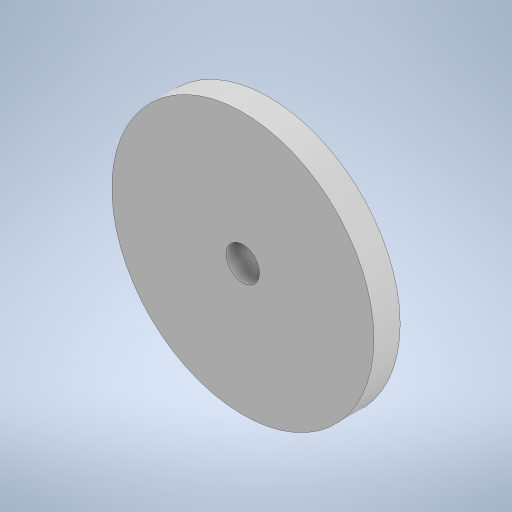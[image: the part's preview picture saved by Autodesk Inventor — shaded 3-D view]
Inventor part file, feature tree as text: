
AUTODESK INVENTOR PART (.ipt)
format: ipt  version: 2024 (Build 280153000, 153)  size: 210,944 bytes
history: native  units: mm
features: extrude x1, sketch x1
ambient origin geometry x8: Origin, YZ Plane, XZ Plane, XY Plane, X Axis, Y Axis, Z Axis, Center Point
bodies: Solid1 (feature_tree)
feature tree (2):
  extrude  "Extrusion1"  Depth=10.0mm
  sketch  "Sketch1"  dims[d0=100.0mm d1=12.7mm d2=10.0mm d3=0.0mm]
